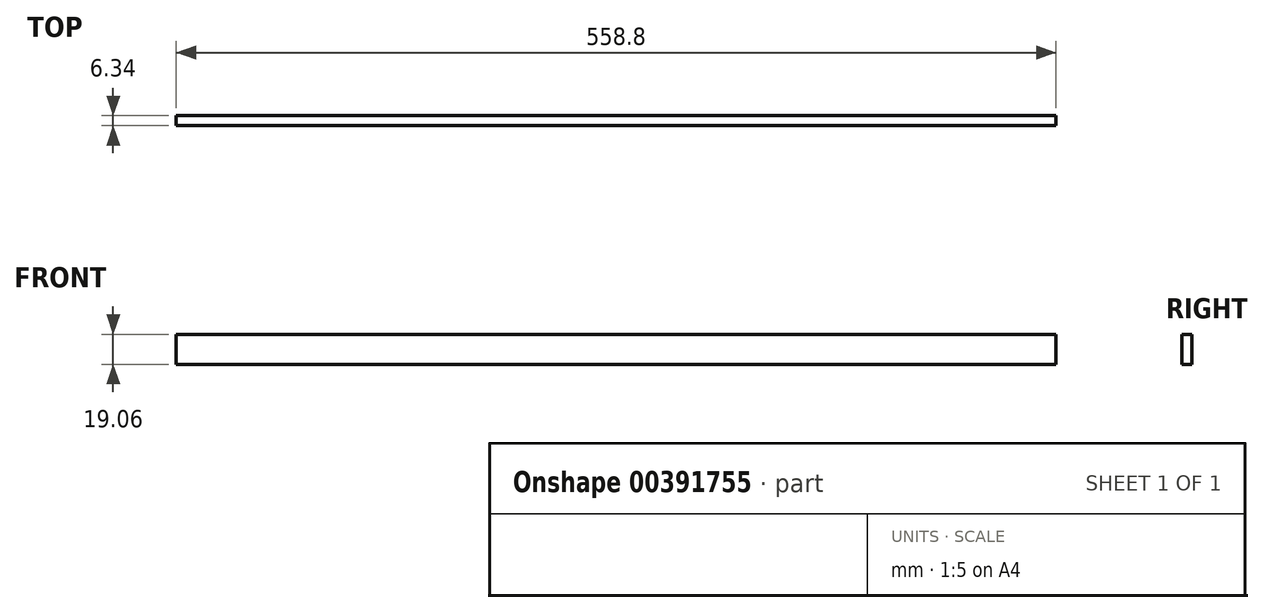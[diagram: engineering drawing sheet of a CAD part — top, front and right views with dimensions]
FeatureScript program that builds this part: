
annotation { "Feature Type Name" : "Feature", "Feature Type Description" : "" }
export const myFeature = defineFeature(function(context is Context, id is Id, definition is map)
    precondition{}
    {
        {
            var Q0;
            Q0=qCreatedBy(makeId("Front.planeOp"),FACE);
            var sketch = newSketch(context, id + "F0", { "sketchPlane" : qUnion([Q0])});
            skLineSegment(sketch, "E0.bottom", {"start": v(279.4, -9.52) * mm, "end": v(-279.4, -9.52) * mm});
            skLineSegment(sketch, "E0.top", {"start": v(279.4, 9.53) * mm, "end": v(-279.4, 9.52) * mm});
            skLineSegment(sketch, "E0.left", {"start": v(279.4, -9.52) * mm, "end": v(279.4, 9.53) * mm});
            skLineSegment(sketch, "E0.right", {"start": v(-279.4, -9.52) * mm, "end": v(-279.4, 9.53) * mm});
            skPoint(sketch, "E0.middle", {"position": v(0, 0) * mm});
            skSolve(sketch);
        }
        {
            var Q0;
            Q0=makeQuery(id+"F0.imprint","IMPRINT",FACE,{"disambiguationData":[TD([[makeQuery(id+"F0.imprint","IMPRINT",EDGE,{"derivedFrom":sQuery(id+"F0.wireOp",EDGE,"E0.bottom")}),-1.0]])]});
            extrude(context, id + "F1", {"entities" : qUnion([Q0]), "endBound" : BoundingType.SYMMETRIC, "depth" : 6.35 * mm});
        }
    });
